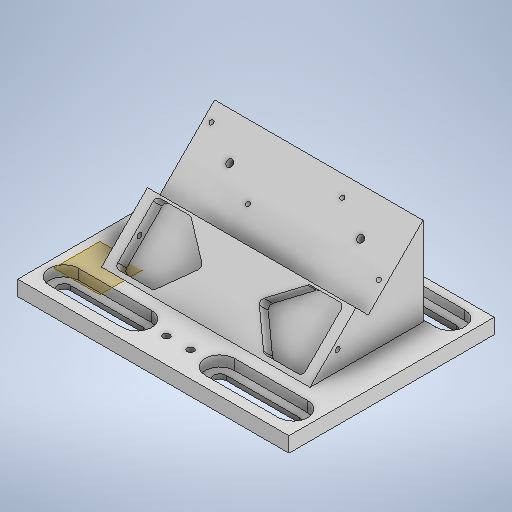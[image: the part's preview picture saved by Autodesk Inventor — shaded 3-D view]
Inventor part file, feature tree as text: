
AUTODESK INVENTOR PART (.ipt)
format: ipt  version: 2025 (Build 290162010, 162A)  size: 536,064 bytes
history: native  units: in
note: dims shown in document units (in); Inventor stores cm internally (conversion verified against a paired STEP export)
features: sketch x18, extrude x12, hole x6, plane x2, fillet x1
ambient origin geometry x8: Origin, YZ Plane, XZ Plane, XY Plane, X Axis, Y Axis, Z Axis, Center Point
bodies: Solid1 (feature_tree)
feature tree (39):
  extrude  "Extrusion1"  Depth=0.9843in
  extrude  "Extrusion2"  Depth=0.2839in
  hole  "Hole1"  [1 undecoded]
  extrude  "Extrusion3"  Depth=0.1935in
  extrude  "Extrusion8"  TaperAngle=90.0deg  [1 undecoded]
  hole  "Hole2"  [1 undecoded]
  hole  "Hole3"  [1 undecoded]
  extrude  "Extrusion10"  Depth=0.2362in TaperAngle=0.0deg
  fillet  "Fillet1"  Radius=1.4173in
  hole  "Hole4"  [1 undecoded]
  hole  "Hole5"  [1 undecoded]
  extrude  "Extrusion11"  Depth=0.5906in
  extrude  "Extrusion12"  TaperAngle=45.0deg  [1 undecoded]
  extrude  "Extrusion13"  Depth=0.7283in
  plane  "Work Plane2"
  extrude  "Extrusion14"  TaperAngle=0.0deg  [1 undecoded]
  extrude  "Extrusion15"  Depth=0.5906in
  plane  "Work Plane1"
  hole  "Hole6"  [1 undecoded]
  extrude  "Extrusion16"  Depth=0.3504in
  extrude  "Extrusion17"  Depth=0.5906in
  sketch  "Sketch1"  dims[d0=0.9843in d1=0.9843in]
  sketch  "Sketch2"  dims[d2=0.2839in d3=4.3307in]
  sketch  "Sketch3"  dims[d4=3.9173in d5=0.0in d6=1.1024in]
  sketch  "Sketch4"  dims[d7=0.6496in d8=1.2402in d10=0.1935in]
  sketch  "Sketch10"  dims[d11=0.0787in d12=90.0deg]
  sketch  "Sketch11"  dims[d13=90.0deg d14=0.0787in]
  sketch  "Sketch12"  dims[d16=0.6496in d18=1.2402in]
  sketch  "Sketch14"  dims[d19=1.1024in d20=0.2362in d21=0.0in d22=1.4173in]
  sketch  "Sketch15"  dims[d23=1.4173in d24=2.4606in]
  sketch  "Sketch16"  dims[d25=0.7283in d26=0.7283in]
  sketch  "Sketch17"  dims[d27=0.1276in d28=0.315in d29=0.1575in d30=0.0787in d31=90.0deg d32=0.5906in d33=0.8108in d34=0.8268in]
  sketch  "Sketch18"  dims[d35=0.3307in d36=0.0in d55=45.0deg]
  sketch  "Sketch19"  dims[d56=0.6496in d57=0.7283in]
  sketch  "Sketch20"  dims[d58=0.2362in d59=0.0in d60=0.0in]
  sketch  "Sketch21"  dims[d61=0.5906in d62=0.5906in]
  sketch  "Sketch22"  dims[d63=0.3504in d64=0.3504in]
  sketch  "Sketch23"  dims[d65=0.3504in d66=0.3504in]
  sketch  "Sketch24"  dims[d67=0.5906in d68=0.5906in d69=0.0787in d70=0.315in d71=0.1575in d72=0.0787in d73=90.0deg d74=0.1575in d75=0.8108in d79=2.9528in d85=0.2362in d86=0.2362in d87=0.5728in d88=0.1724in d89=0.5635in d90=0.1969in d91=0.8108in d95=0.4724in d96=0.0in d97=0.0in d98=0.0787in d101=0.1181in d102=0.6024in d103=0.0968in d104=0.2362in d105=0.3701in d106=0.1724in d107=90.0deg d108=0.3465in d109=0.8108in d110=0.1181in d111=0.6024in d112=0.0968in d113=0.2362in d114=0.248in d115=0.0787in d116=90.0deg d117=0.3465in d118=0.8108in d119=0.1935in d120=0.7283in d121=0.748in d122=0.5906in d123=0.5906in d124=0.9514in d125=0.9514in d126=0.5906in d127=0.748in d128=0.5906in d129=0.2839in d130=0.0in d131=0.2756in d132=0.2756in d133=0.3543in d134=0.2756in d135=0.3937in d136=2.6772in d138=2.9528in d139=2.9528in d140=0.1724in d141=0.0in d142=0.1181in d143=0.1181in d144=0.0in d145=0.0in d153=2.9528in d154=2.9528in d155=0.3937in d156=0.3937in d157=0.2756in d158=0.2756in d159=1.378in d160=1.378in d161=0.1969in d162=0.0in d163=0.1181in d164=0.1181in d165=0.0in d166=0.0in d167=0.4724in d168=0.4724in d169=2.3228in d170=2.3228in d171=0.1276in d172=0.315in d173=0.1575in d174=0.0787in d175=90.0deg d176=0.4646in d177=0.8108in d178=0.2839in d179=2.1589in d180=0.5906in d181=0.0in d182=0.2839in d183=2.1589in d184=0.5906in d185=0.0in]
note: 9 required parameter values undecoded (feature->parameter linkage not recoverable at this tier; creation-order binding heuristic only, values carry confidence <= 0.55)
